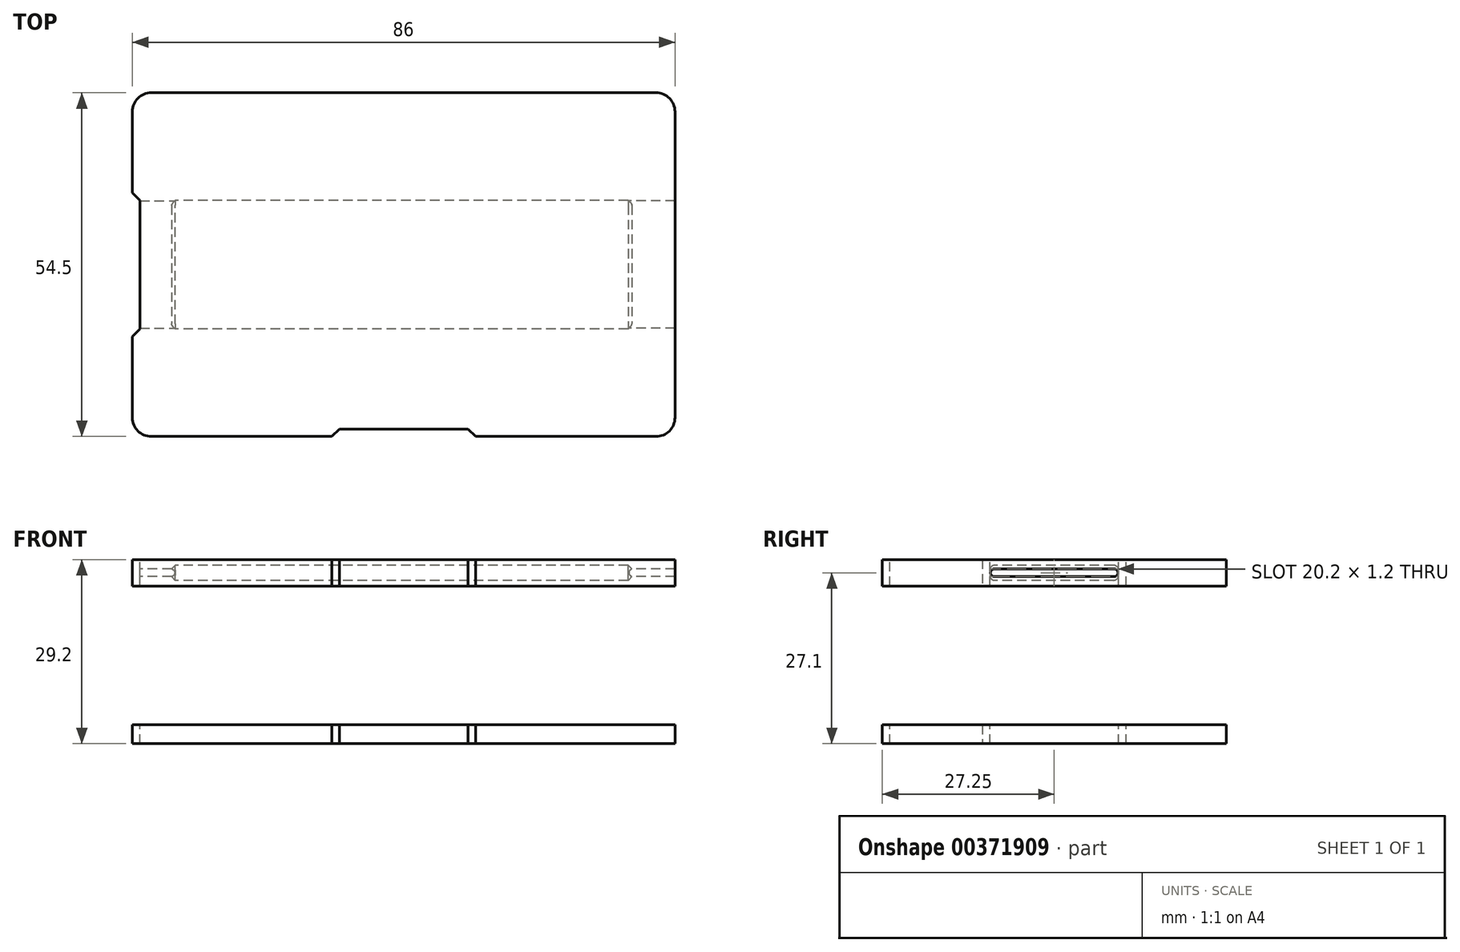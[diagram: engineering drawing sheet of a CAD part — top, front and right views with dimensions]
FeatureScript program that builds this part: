
annotation { "Feature Type Name" : "Feature", "Feature Type Description" : "" }
export const myFeature = defineFeature(function(context is Context, id is Id, definition is map)
    precondition{}
    {
        {
            var Q0;
            Q0=qCreatedBy(makeId("Top.planeOp"),FACE);
            var sketch = newSketch(context, id + "F0", { "sketchPlane" : qUnion([Q0])});
            skLineSegment(sketch, "E0.bottom", {"start": v(-40, 27.25) * mm, "end": v(40, 27.25) * mm});
            skLineSegment(sketch, "E0.top", {"start": v(-40, -27.25) * mm, "end": v(40, -27.25) * mm});
            skLineSegment(sketch, "E0.left", {"start": v(-43, 24.25) * mm, "end": v(-43, -24.25) * mm});
            skLineSegment(sketch, "E0.right", {"start": v(43, 24.25) * mm, "end": v(43, -24.25) * mm});
            skPoint(sketch, "E0.middle", {"position": v(0, 0) * mm});
            skPoint(sketch, "E1.visualSharp", {"position": v(-43, 27.25) * mm});
            skArc(sketch, "E1.filletArc", {"start": v(-40, 27.25) * mm, "mid": v(-42.12, 26.37) * mm, "end": v(-43, 24.25) * mm});
            skPoint(sketch, "E2.visualSharp", {"position": v(43, 27.25) * mm});
            skArc(sketch, "E2.filletArc", {"start": v(43, 24.25) * mm, "mid": v(42.12, 26.37) * mm, "end": v(40, 27.25) * mm});
            skPoint(sketch, "E3.visualSharp", {"position": v(-43, -27.25) * mm});
            skArc(sketch, "E3.filletArc", {"start": v(-43, -24.25) * mm, "mid": v(-42.12, -26.37) * mm, "end": v(-40, -27.25) * mm});
            skPoint(sketch, "E4.visualSharp", {"position": v(43, -27.25) * mm});
            skArc(sketch, "E4.filletArc", {"start": v(40, -27.25) * mm, "mid": v(42.12, -26.37) * mm, "end": v(43, -24.25) * mm});
            skSolve(sketch);
        }
        {
            var Q0;
            Q0 = qSketchRegion(id + "F0", true);
            extrude(context, id + "F1", {"entities" : qUnion([Q0]), "depth" : 3 * mm});
        }
        {
            var Q0;
            Q0=qCreatedBy(makeId("Top.planeOp"),FACE);
            cPlane(context, id + "F2", {"entities" : qUnion([Q0]), "cplaneType" : CPlaneType.OFFSET, "offset" : 25 * mm, "width" : 150 * mm, "height" : 150 * mm});
        }
        {
            var Q0;
            Q0=qCreatedBy(id+"F2.planeOp",FACE);
            var sketch = newSketch(context, id + "F3", { "sketchPlane" : qUnion([Q0])});
            skArc(sketch, "E5.0.0", {"start": v(-43, -24.25) * mm, "mid": v(-42.12, -26.37) * mm, "end": v(-40, -27.25) * mm});
            skLineSegment(sketch, "E5.0.1", {"start": v(-40, -27.25) * mm, "end": v(40, -27.25) * mm});
            skArc(sketch, "E5.0.2", {"start": v(40, -27.25) * mm, "mid": v(42.12, -26.37) * mm, "end": v(43, -24.25) * mm});
            skLineSegment(sketch, "E5.0.3", {"start": v(43, -24.25) * mm, "end": v(43, 24.25) * mm});
            skArc(sketch, "E5.0.4", {"start": v(43, 24.25) * mm, "mid": v(42.12, 26.37) * mm, "end": v(40, 27.25) * mm});
            skLineSegment(sketch, "E5.0.5", {"start": v(40, 27.25) * mm, "end": v(-40, 27.25) * mm});
            skArc(sketch, "E5.0.6", {"start": v(-40, 27.25) * mm, "mid": v(-42.12, 26.37) * mm, "end": v(-43, 24.25) * mm});
            skLineSegment(sketch, "E5.0.7", {"start": v(-43, 24.25) * mm, "end": v(-43, -24.25) * mm});
            skSolve(sketch);
        }
        {
            var Q0;
            Q0 = qSketchRegion(id + "F3", true);
            extrude(context, id + "F4", {"entities" : qUnion([Q0]), "depth" : 4.2 * mm});
        }
        {
            var Q0;
            Q0=makeQuery(id+"F4.opExtrude","CAP_FACE",FACE,{"disambiguationData":[OSD([sQuery(id+"F3.wireOp",EDGE,"E5.0.0"),sQuery(id+"F3.wireOp",EDGE,"E5.0.1"),sQuery(id+"F3.wireOp",EDGE,"E5.0.2"),sQuery(id+"F3.wireOp",EDGE,"E5.0.3"),sQuery(id+"F3.wireOp",EDGE,"E5.0.4"),sQuery(id+"F3.wireOp",EDGE,"E5.0.5"),sQuery(id+"F3.wireOp",EDGE,"E5.0.6"),sQuery(id+"F3.wireOp",EDGE,"E5.0.7")])],"isStart":false});
            var sketch = newSketch(context, id + "F5", { "sketchPlane" : qUnion([Q0])});
            skLineSegment(sketch, "E6.bottom", {"start": v(-41.8, -10.2) * mm, "end": v(-44.2, -10.2) * mm});
            skLineSegment(sketch, "E6.top", {"start": v(-41.8, 10.2) * mm, "end": v(-44.2, 10.2) * mm});
            skLineSegment(sketch, "E6.left", {"start": v(-41.8, -10.2) * mm, "end": v(-41.8, 10.2) * mm});
            skLineSegment(sketch, "E6.right", {"start": v(-44.2, -10.2) * mm, "end": v(-44.2, 10.2) * mm});
            skPoint(sketch, "E6.middle", {"position": v(-43, 0) * mm});
            skSolve(sketch);
        }
        {
            var Q0;
            Q0 = qSketchRegion(id + "F5", true);
            extrude(context, id + "F6", {"entities" : qUnion([Q0]), "operationType" : NewBodyOperationType.REMOVE, "oppositeDirection" : true, "depth" : 30.2 * mm});
        }
        {
            var Q0;
            Q0=makeQuery(id+"F4.opExtrude","CAP_FACE",FACE,{"disambiguationData":[OSD([sQuery(id+"F3.wireOp",EDGE,"E5.0.0"),sQuery(id+"F3.wireOp",EDGE,"E5.0.1"),sQuery(id+"F3.wireOp",EDGE,"E5.0.2"),sQuery(id+"F3.wireOp",EDGE,"E5.0.3"),sQuery(id+"F3.wireOp",EDGE,"E5.0.4"),sQuery(id+"F3.wireOp",EDGE,"E5.0.5"),sQuery(id+"F3.wireOp",EDGE,"E5.0.6"),sQuery(id+"F3.wireOp",EDGE,"E5.0.7")])],"isStart":false});
            var sketch = newSketch(context, id + "F7", { "sketchPlane" : qUnion([Q0])});
            skLineSegment(sketch, "E7.bottom", {"start": v(-10.2, -26.05) * mm, "end": v(10.2, -26.05) * mm});
            skLineSegment(sketch, "E7.top", {"start": v(-10.2, -28.45) * mm, "end": v(10.2, -28.45) * mm});
            skLineSegment(sketch, "E7.left", {"start": v(-10.2, -26.05) * mm, "end": v(-10.2, -28.45) * mm});
            skLineSegment(sketch, "E7.right", {"start": v(10.2, -26.05) * mm, "end": v(10.2, -28.45) * mm});
            skPoint(sketch, "E7.middle", {"position": v(0, -27.25) * mm});
            skSolve(sketch);
        }
        {
            var Q0;
            Q0 = qSketchRegion(id + "F7", true);
            extrude(context, id + "F8", {"entities" : qUnion([Q0]), "operationType" : NewBodyOperationType.REMOVE, "oppositeDirection" : true, "depth" : 31.7 * mm});
        }
        {
            var Q0;
            {var subQ0=sQuery(id+"F3.wireOp",EDGE,"E5.0.7");var subQ1=sQuery(id+"F3.wireOp",EDGE,"E5.0.6");var subQ2=sQuery(id+"F3.wireOp",EDGE,"E5.0.5");var subQ3=sQuery(id+"F3.wireOp",EDGE,"E5.0.4");var subQ4=sQuery(id+"F3.wireOp",EDGE,"E5.0.3");var subQ5=sQuery(id+"F3.wireOp",EDGE,"E5.0.2");var subQ6=sQuery(id+"F3.wireOp",EDGE,"E5.0.1");var subQ7=sQuery(id+"F3.wireOp",EDGE,"E5.0.0");Q0=makeQuery(id+"F6.boolean.opBoolean","COPY",FACE,{"disambiguationData":[TD([makeQuery(id+"F4.opExtrude","CAP_FACE",FACE,{"disambiguationData":[OSD([subQ7,subQ6,subQ5,subQ4,subQ3,subQ2,subQ1,subQ0])],"isStart":true})])],"derivedFrom":makeQuery(id+"F6.opExtrude","SWEPT_FACE",FACE,{"disambiguationData":[OSD([sQuery(id+"F5.wireOp",EDGE,"E6.left")])]})});}
            var sketch = newSketch(context, id + "F9", { "sketchPlane" : qUnion([Q0])});
            skLineSegment(sketch, "E8.bottom", {"start": v(-10.1, 27.7) * mm, "end": v(10.1, 27.7) * mm});
            skLineSegment(sketch, "E8.top", {"start": v(-10.1, 26.5) * mm, "end": v(10.1, 26.5) * mm});
            skLineSegment(sketch, "E8.left", {"start": v(-10.1, 27.7) * mm, "end": v(-10.1, 26.5) * mm});
            skLineSegment(sketch, "E8.right", {"start": v(10.1, 27.7) * mm, "end": v(10.1, 26.5) * mm});
            skPoint(sketch, "E8.middle", {"position": v(0, 27.1) * mm});
            skPoint(sketch, "E8.middle.positionSnap0", {"position": v(-10.2, 27.1) * mm});
            skPoint(sketch, "E8.middle.positionSnap1", {"position": v(0, 25) * mm});
            skPoint(sketch, "E8.centerSnap0", {"position": v(-10.2, 27.1) * mm});
            skPoint(sketch, "E8.centerSnap1", {"position": v(0, 25) * mm});
            skSolve(sketch);
        }
        {
            var Q0;
            Q0=makeQuery(id+"F6.boolean.opBoolean","INTERSECT",EDGE,{"derivedFrom":[makeQuery(id+"F4.opExtrude","SWEPT_FACE",FACE,{"disambiguationData":[OSD([sQuery(id+"F3.wireOp",EDGE,"E5.0.7")])]}),makeQuery(id+"F6.opExtrude","SWEPT_FACE",FACE,{"disambiguationData":[OSD([sQuery(id+"F5.wireOp",EDGE,"E6.top")])]})]});
            var Q1;
            Q1=makeQuery(id+"F6.boolean.opBoolean","INTERSECT",EDGE,{"derivedFrom":[makeQuery(id+"F4.opExtrude","SWEPT_FACE",FACE,{"disambiguationData":[OSD([sQuery(id+"F3.wireOp",EDGE,"E5.0.7")])]}),makeQuery(id+"F6.opExtrude","SWEPT_FACE",FACE,{"disambiguationData":[OSD([sQuery(id+"F5.wireOp",EDGE,"E6.bottom")])]})]});
            var Q2;
            Q2=makeQuery(id+"F6.boolean.opBoolean","INTERSECT",EDGE,{"derivedFrom":[makeQuery(id+"F1.opExtrude","SWEPT_FACE",FACE,{"disambiguationData":[OSD([sQuery(id+"F0.wireOp",EDGE,"E0.left")])]}),makeQuery(id+"F6.opExtrude","SWEPT_FACE",FACE,{"disambiguationData":[OSD([sQuery(id+"F5.wireOp",EDGE,"E6.top")])]})]});
            var Q3;
            Q3=makeQuery(id+"F6.boolean.opBoolean","INTERSECT",EDGE,{"derivedFrom":[makeQuery(id+"F1.opExtrude","SWEPT_FACE",FACE,{"disambiguationData":[OSD([sQuery(id+"F0.wireOp",EDGE,"E0.left")])]}),makeQuery(id+"F6.opExtrude","SWEPT_FACE",FACE,{"disambiguationData":[OSD([sQuery(id+"F5.wireOp",EDGE,"E6.bottom")])]})]});
            var Q4;
            Q4=makeQuery(id+"FuwmC8ETssg1GWK_2.1.F6.boolean.opBoolean","INTERSECT",EDGE,{"derivedFrom":[makeQuery(id+"F4.opExtrude","SWEPT_FACE",FACE,{"disambiguationData":[OSD([sQuery(id+"F3.wireOp",EDGE,"E5.0.3")])]}),makeQuery(id+"FuwmC8ETssg1GWK_2.1.F6.opExtrude","SWEPT_FACE",FACE,{"disambiguationData":[OSD([sQuery(id+"F5.wireOp",EDGE,"E6.top")])]})]});
            var Q5;
            Q5=makeQuery(id+"FuwmC8ETssg1GWK_2.1.F6.boolean.opBoolean","INTERSECT",EDGE,{"derivedFrom":[makeQuery(id+"F4.opExtrude","SWEPT_FACE",FACE,{"disambiguationData":[OSD([sQuery(id+"F3.wireOp",EDGE,"E5.0.3")])]}),makeQuery(id+"FuwmC8ETssg1GWK_2.1.F6.opExtrude","SWEPT_FACE",FACE,{"disambiguationData":[OSD([sQuery(id+"F5.wireOp",EDGE,"E6.bottom")])]})]});
            var Q6;
            Q6=makeQuery(id+"FuwmC8ETssg1GWK_2.1.F6.boolean.opBoolean","INTERSECT",EDGE,{"derivedFrom":[makeQuery(id+"F1.opExtrude","SWEPT_FACE",FACE,{"disambiguationData":[OSD([sQuery(id+"F0.wireOp",EDGE,"E0.right")])]}),makeQuery(id+"FuwmC8ETssg1GWK_2.1.F6.opExtrude","SWEPT_FACE",FACE,{"disambiguationData":[OSD([sQuery(id+"F5.wireOp",EDGE,"E6.top")])]})]});
            var Q7;
            Q7=makeQuery(id+"FuwmC8ETssg1GWK_2.1.F6.boolean.opBoolean","INTERSECT",EDGE,{"derivedFrom":[makeQuery(id+"F1.opExtrude","SWEPT_FACE",FACE,{"disambiguationData":[OSD([sQuery(id+"F0.wireOp",EDGE,"E0.right")])]}),makeQuery(id+"FuwmC8ETssg1GWK_2.1.F6.opExtrude","SWEPT_FACE",FACE,{"disambiguationData":[OSD([sQuery(id+"F5.wireOp",EDGE,"E6.bottom")])]})]});
            var Q8;
            Q8=makeQuery(id+"F8.boolean.opBoolean","INTERSECT",EDGE,{"derivedFrom":[makeQuery(id+"F1.opExtrude","SWEPT_FACE",FACE,{"disambiguationData":[OSD([sQuery(id+"F0.wireOp",EDGE,"E0.top")])]}),makeQuery(id+"F8.opExtrude","SWEPT_FACE",FACE,{"disambiguationData":[OSD([sQuery(id+"F7.wireOp",EDGE,"E7.left")])]})]});
            var Q9;
            Q9=makeQuery(id+"F8.boolean.opBoolean","INTERSECT",EDGE,{"derivedFrom":[makeQuery(id+"F4.opExtrude","SWEPT_FACE",FACE,{"disambiguationData":[OSD([sQuery(id+"F3.wireOp",EDGE,"E5.0.1")])]}),makeQuery(id+"F8.opExtrude","SWEPT_FACE",FACE,{"disambiguationData":[OSD([sQuery(id+"F7.wireOp",EDGE,"E7.left")])]})]});
            var Q10;
            Q10=makeQuery(id+"F8.boolean.opBoolean","INTERSECT",EDGE,{"derivedFrom":[makeQuery(id+"F4.opExtrude","SWEPT_FACE",FACE,{"disambiguationData":[OSD([sQuery(id+"F3.wireOp",EDGE,"E5.0.1")])]}),makeQuery(id+"F8.opExtrude","SWEPT_FACE",FACE,{"disambiguationData":[OSD([sQuery(id+"F7.wireOp",EDGE,"E7.right")])]})]});
            var Q11;
            Q11=makeQuery(id+"F8.boolean.opBoolean","INTERSECT",EDGE,{"derivedFrom":[makeQuery(id+"F1.opExtrude","SWEPT_FACE",FACE,{"disambiguationData":[OSD([sQuery(id+"F0.wireOp",EDGE,"E0.top")])]}),makeQuery(id+"F8.opExtrude","SWEPT_FACE",FACE,{"disambiguationData":[OSD([sQuery(id+"F7.wireOp",EDGE,"E7.right")])]})]});
            chamfer(context, id + "F10", {"entities" : qUnion([Q0, Q1, Q2, Q3, Q4, Q5, Q6, Q7, Q8, Q9, Q10, Q11]), "width" : 1.2 * mm, "tangentPropagation" : true});
        }
        {
            var Q0;
            {var subQ0=sQuery(id+"F3.wireOp",EDGE,"E5.0.7");var subQ1=sQuery(id+"F3.wireOp",EDGE,"E5.0.6");var subQ2=sQuery(id+"F3.wireOp",EDGE,"E5.0.5");var subQ3=sQuery(id+"F3.wireOp",EDGE,"E5.0.4");var subQ4=sQuery(id+"F3.wireOp",EDGE,"E5.0.3");var subQ5=sQuery(id+"F3.wireOp",EDGE,"E5.0.2");var subQ6=sQuery(id+"F3.wireOp",EDGE,"E5.0.1");var subQ7=sQuery(id+"F3.wireOp",EDGE,"E5.0.0");Q0=makeQuery(id+"F6.boolean.opBoolean","COPY",FACE,{"disambiguationData":[TD([makeQuery(id+"F4.opExtrude","CAP_FACE",FACE,{"disambiguationData":[OSD([subQ7,subQ6,subQ5,subQ4,subQ3,subQ2,subQ1,subQ0])],"isStart":true})])],"derivedFrom":makeQuery(id+"F6.opExtrude","SWEPT_FACE",FACE,{"disambiguationData":[OSD([sQuery(id+"F5.wireOp",EDGE,"E6.left")])]})});}
            var sketch = newSketch(context, id + "F11", { "sketchPlane" : qUnion([Q0])});
            skLineSegment(sketch, "E9.bottom", {"start": v(-10.2, 28.3) * mm, "end": v(10.2, 28.3) * mm});
            skLineSegment(sketch, "E9.top", {"start": v(-10.2, 25.9) * mm, "end": v(10.2, 25.9) * mm});
            skLineSegment(sketch, "E9.left", {"start": v(-10.2, 28.3) * mm, "end": v(-10.2, 25.9) * mm});
            skLineSegment(sketch, "E9.right", {"start": v(10.2, 28.3) * mm, "end": v(10.2, 25.9) * mm});
            skPoint(sketch, "E9.middle", {"position": v(0, 27.1) * mm});
            skPoint(sketch, "E9.middle.positionSnap0", {"position": v(0, 26.5) * mm});
            skPoint(sketch, "E9.middle.positionSnap1", {"position": v(-10.1, 27.1) * mm});
            skPoint(sketch, "E9.centerSnap0", {"position": v(0, 26.5) * mm});
            skPoint(sketch, "E9.centerSnap1", {"position": v(-10.1, 27.1) * mm});
            skSolve(sketch);
        }
        {
            var Q0;
            Q0=makeQuery(id+"F11.imprint","IMPRINT",FACE,{"disambiguationData":[TD([[makeQuery(id+"F11.imprint","IMPRINT",EDGE,{"derivedFrom":sQuery(id+"F11.wireOp",EDGE,"E9.bottom")}),-1.0]])]});
            extrude(context, id + "F12", {"entities" : qUnion([Q0]), "operationType" : NewBodyOperationType.REMOVE, "oppositeDirection" : true, "depth" : 78 * mm, "hasSecondDirection" : true, "secondDirectionOppositeDirection" : true, "secondDirectionDepth" : 5 * mm});
        }
        {
            var Q0;
            Q0=makeQuery(id+"F9.imprint","IMPRINT",FACE,{"disambiguationData":[TD([[makeQuery(id+"F9.imprint","IMPRINT",EDGE,{"derivedFrom":sQuery(id+"F9.wireOp",EDGE,"E8.bottom")}),-1.0]])]});
            extrude(context, id + "F13", {"entities" : qUnion([Q0]), "operationType" : NewBodyOperationType.REMOVE, "oppositeDirection" : true, "depth" : 104.6 * mm});
        }
        {
            var Q0;
            {var subQ8=sQuery(id+"F9.wireOp",EDGE,"E8.top");var subQ9=sQuery(id+"F9.wireOp",EDGE,"E8.left");Q0=makeQuery(id+"F13.boolean.opBoolean","COPY",EDGE,{"disambiguationData":[TD([makeQuery(id+"F12.boolean.opBoolean","COPY",FACE,{"derivedFrom":makeQuery(id+"F12.opExtrude","CAP_FACE",FACE,{"disambiguationData":[OSD([sQuery(id+"F11.wireOp",EDGE,"E9.bottom"),sQuery(id+"F11.wireOp",EDGE,"E9.top"),sQuery(id+"F11.wireOp",EDGE,"E9.left"),sQuery(id+"F11.wireOp",EDGE,"E9.right")])],"isStart":true})})])],"derivedFrom":makeQuery(id+"F13.opExtrude","SWEPT_EDGE",EDGE,{"disambiguationData":[OSD([subQ8,subQ9])]})});}
            var Q1;
            {var subQ8=sQuery(id+"F9.wireOp",EDGE,"E8.bottom");var subQ9=sQuery(id+"F9.wireOp",EDGE,"E8.left");Q1=makeQuery(id+"F13.boolean.opBoolean","COPY",EDGE,{"disambiguationData":[TD([makeQuery(id+"F12.boolean.opBoolean","COPY",FACE,{"derivedFrom":makeQuery(id+"F12.opExtrude","CAP_FACE",FACE,{"disambiguationData":[OSD([sQuery(id+"F11.wireOp",EDGE,"E9.bottom"),sQuery(id+"F11.wireOp",EDGE,"E9.top"),sQuery(id+"F11.wireOp",EDGE,"E9.left"),sQuery(id+"F11.wireOp",EDGE,"E9.right")])],"isStart":true})})])],"derivedFrom":makeQuery(id+"F13.opExtrude","SWEPT_EDGE",EDGE,{"disambiguationData":[OSD([subQ8,subQ9])]})});}
            var Q2;
            {var subQ8=sQuery(id+"F9.wireOp",EDGE,"E8.bottom");var subQ9=sQuery(id+"F9.wireOp",EDGE,"E8.right");Q2=makeQuery(id+"F13.boolean.opBoolean","COPY",EDGE,{"disambiguationData":[TD([makeQuery(id+"F12.boolean.opBoolean","COPY",FACE,{"derivedFrom":makeQuery(id+"F12.opExtrude","CAP_FACE",FACE,{"disambiguationData":[OSD([sQuery(id+"F11.wireOp",EDGE,"E9.bottom"),sQuery(id+"F11.wireOp",EDGE,"E9.top"),sQuery(id+"F11.wireOp",EDGE,"E9.left"),sQuery(id+"F11.wireOp",EDGE,"E9.right")])],"isStart":true})})])],"derivedFrom":makeQuery(id+"F13.opExtrude","SWEPT_EDGE",EDGE,{"disambiguationData":[OSD([subQ8,subQ9])]})});}
            var Q3;
            {var subQ8=sQuery(id+"F9.wireOp",EDGE,"E8.top");var subQ9=sQuery(id+"F9.wireOp",EDGE,"E8.right");Q3=makeQuery(id+"F13.boolean.opBoolean","COPY",EDGE,{"disambiguationData":[TD([makeQuery(id+"F12.boolean.opBoolean","COPY",FACE,{"derivedFrom":makeQuery(id+"F12.opExtrude","CAP_FACE",FACE,{"disambiguationData":[OSD([sQuery(id+"F11.wireOp",EDGE,"E9.bottom"),sQuery(id+"F11.wireOp",EDGE,"E9.top"),sQuery(id+"F11.wireOp",EDGE,"E9.left"),sQuery(id+"F11.wireOp",EDGE,"E9.right")])],"isStart":true})})])],"derivedFrom":makeQuery(id+"F13.opExtrude","SWEPT_EDGE",EDGE,{"disambiguationData":[OSD([subQ8,subQ9])]})});}
            var Q4;
            {var subQ8=sQuery(id+"F9.wireOp",EDGE,"E8.bottom");var subQ9=sQuery(id+"F9.wireOp",EDGE,"E8.left");Q4=makeQuery(id+"F13.boolean.opBoolean","COPY",EDGE,{"disambiguationData":[TD([makeQuery(id+"F12.boolean.opBoolean","COPY",FACE,{"derivedFrom":makeQuery(id+"F12.opExtrude","CAP_FACE",FACE,{"disambiguationData":[OSD([sQuery(id+"F11.wireOp",EDGE,"E9.bottom"),sQuery(id+"F11.wireOp",EDGE,"E9.top"),sQuery(id+"F11.wireOp",EDGE,"E9.left"),sQuery(id+"F11.wireOp",EDGE,"E9.right")])],"isStart":false})})])],"derivedFrom":makeQuery(id+"F13.opExtrude","SWEPT_EDGE",EDGE,{"disambiguationData":[OSD([subQ8,subQ9])]})});}
            var Q5;
            {var subQ8=sQuery(id+"F9.wireOp",EDGE,"E8.top");var subQ9=sQuery(id+"F9.wireOp",EDGE,"E8.left");Q5=makeQuery(id+"F13.boolean.opBoolean","COPY",EDGE,{"disambiguationData":[TD([makeQuery(id+"F12.boolean.opBoolean","COPY",FACE,{"derivedFrom":makeQuery(id+"F12.opExtrude","CAP_FACE",FACE,{"disambiguationData":[OSD([sQuery(id+"F11.wireOp",EDGE,"E9.bottom"),sQuery(id+"F11.wireOp",EDGE,"E9.top"),sQuery(id+"F11.wireOp",EDGE,"E9.left"),sQuery(id+"F11.wireOp",EDGE,"E9.right")])],"isStart":false})})])],"derivedFrom":makeQuery(id+"F13.opExtrude","SWEPT_EDGE",EDGE,{"disambiguationData":[OSD([subQ8,subQ9])]})});}
            var Q6;
            {var subQ8=sQuery(id+"F9.wireOp",EDGE,"E8.right");var subQ9=sQuery(id+"F9.wireOp",EDGE,"E8.top");Q6=makeQuery(id+"F13.boolean.opBoolean","COPY",EDGE,{"disambiguationData":[TD([makeQuery(id+"F12.boolean.opBoolean","COPY",FACE,{"derivedFrom":makeQuery(id+"F12.opExtrude","CAP_FACE",FACE,{"disambiguationData":[OSD([sQuery(id+"F11.wireOp",EDGE,"E9.bottom"),sQuery(id+"F11.wireOp",EDGE,"E9.top"),sQuery(id+"F11.wireOp",EDGE,"E9.left"),sQuery(id+"F11.wireOp",EDGE,"E9.right")])],"isStart":false})})])],"derivedFrom":makeQuery(id+"F13.opExtrude","SWEPT_EDGE",EDGE,{"disambiguationData":[OSD([subQ9,subQ8])]})});}
            var Q7;
            {var subQ8=sQuery(id+"F9.wireOp",EDGE,"E8.bottom");var subQ9=sQuery(id+"F9.wireOp",EDGE,"E8.right");Q7=makeQuery(id+"F13.boolean.opBoolean","COPY",EDGE,{"disambiguationData":[TD([makeQuery(id+"F12.boolean.opBoolean","COPY",FACE,{"derivedFrom":makeQuery(id+"F12.opExtrude","CAP_FACE",FACE,{"disambiguationData":[OSD([sQuery(id+"F11.wireOp",EDGE,"E9.bottom"),sQuery(id+"F11.wireOp",EDGE,"E9.top"),sQuery(id+"F11.wireOp",EDGE,"E9.left"),sQuery(id+"F11.wireOp",EDGE,"E9.right")])],"isStart":false})})])],"derivedFrom":makeQuery(id+"F13.opExtrude","SWEPT_EDGE",EDGE,{"disambiguationData":[OSD([subQ8,subQ9])]})});}
            fillet(context, id + "F14", {"entities" : qUnion([Q0, Q1, Q2, Q3, Q4, Q5, Q6, Q7]), "radius" : 0.6 * mm, "tangentPropagation" : true, "allowEdgeOverflow" : false});
        }
        {
            var Q0;
            Q0=makeQuery(id+"F12.boolean.opBoolean","COPY",EDGE,{"derivedFrom":makeQuery(id+"F12.opExtrude","SWEPT_EDGE",EDGE,{"disambiguationData":[OSD([sQuery(id+"F3.wireOp",EDGE,"E5.0.7"),sQuery(id+"F5.wireOp",EDGE,"E6.top"),sQuery(id+"F5.wireOp",EDGE,"E6.left"),sQuery(id+"F11.wireOp",EDGE,"E9.bottom"),sQuery(id+"F11.wireOp",EDGE,"E9.left")])]})});
            var Q1;
            Q1=makeQuery(id+"F12.boolean.opBoolean","COPY",EDGE,{"derivedFrom":makeQuery(id+"F12.opExtrude","SWEPT_EDGE",EDGE,{"disambiguationData":[OSD([sQuery(id+"F3.wireOp",EDGE,"E5.0.7"),sQuery(id+"F5.wireOp",EDGE,"E6.top"),sQuery(id+"F5.wireOp",EDGE,"E6.left"),sQuery(id+"F11.wireOp",EDGE,"E9.top"),sQuery(id+"F11.wireOp",EDGE,"E9.left")])]})});
            var Q2;
            Q2=makeQuery(id+"F12.boolean.opBoolean","COPY",EDGE,{"derivedFrom":makeQuery(id+"F12.opExtrude","SWEPT_EDGE",EDGE,{"disambiguationData":[OSD([sQuery(id+"F3.wireOp",EDGE,"E5.0.7"),sQuery(id+"F5.wireOp",EDGE,"E6.bottom"),sQuery(id+"F5.wireOp",EDGE,"E6.left"),sQuery(id+"F11.wireOp",EDGE,"E9.bottom"),sQuery(id+"F11.wireOp",EDGE,"E9.right")])]})});
            var Q3;
            Q3=makeQuery(id+"F12.boolean.opBoolean","COPY",EDGE,{"derivedFrom":makeQuery(id+"F12.opExtrude","SWEPT_EDGE",EDGE,{"disambiguationData":[OSD([sQuery(id+"F3.wireOp",EDGE,"E5.0.7"),sQuery(id+"F5.wireOp",EDGE,"E6.bottom"),sQuery(id+"F5.wireOp",EDGE,"E6.left"),sQuery(id+"F11.wireOp",EDGE,"E9.top"),sQuery(id+"F11.wireOp",EDGE,"E9.right")])]})});
            fillet(context, id + "F15", {"entities" : qUnion([Q0, Q1, Q2, Q3]), "radius" : 0.8 * mm, "tangentPropagation" : true, "allowEdgeOverflow" : false});
        }
        {
            var Q0;
            Q0=makeQuery(id+"F12.boolean.opBoolean","COPY",EDGE,{"derivedFrom":makeQuery(id+"F12.opExtrude","CAP_EDGE",EDGE,{"disambiguationData":[OSD([sQuery(id+"F11.wireOp",EDGE,"E9.top")])],"isStart":false})});
            var Q1;
            Q1=makeQuery(id+"F12.boolean.opBoolean","COPY",EDGE,{"derivedFrom":makeQuery(id+"F12.opExtrude","CAP_EDGE",EDGE,{"disambiguationData":[OSD([sQuery(id+"F11.wireOp",EDGE,"E9.bottom")])],"isStart":true})});
            chamfer(context, id + "F16", {"entities" : qUnion([Q0, Q1]), "width" : 0.6 * mm, "tangentPropagation" : true});
        }
    });
